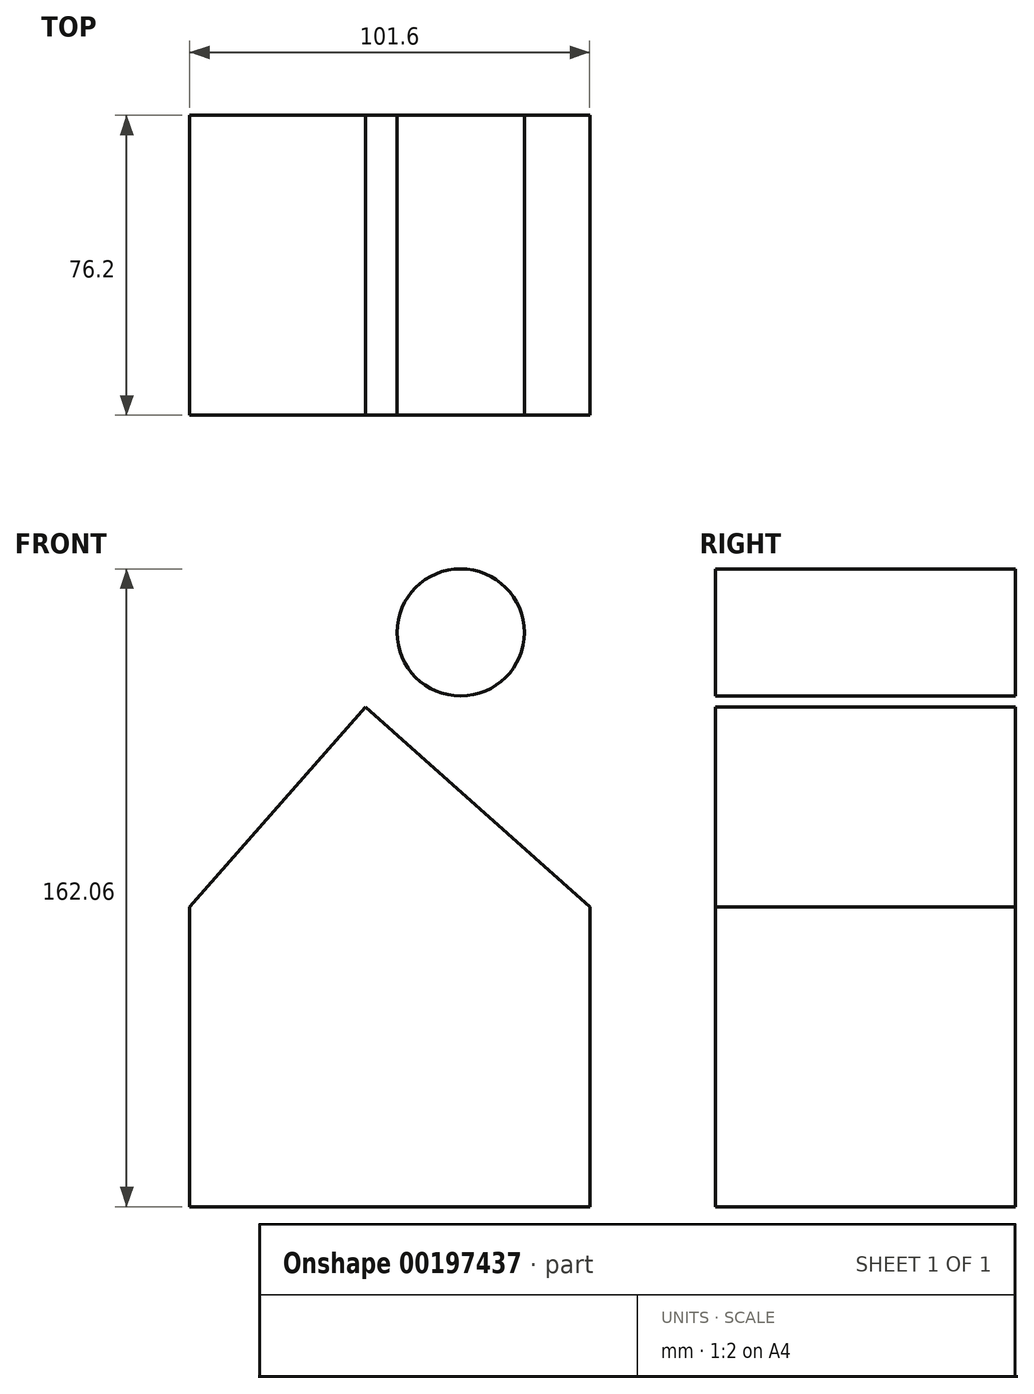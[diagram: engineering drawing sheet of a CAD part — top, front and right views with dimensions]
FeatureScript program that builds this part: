
annotation { "Feature Type Name" : "Feature", "Feature Type Description" : "" }
export const myFeature = defineFeature(function(context is Context, id is Id, definition is map)
    precondition{}
    {
        {
            var Q0;
            Q0=qCreatedBy(makeId("Front.planeOp"),FACE);
            var sketch = newSketch(context, id + "F0", { "sketchPlane" : qUnion([Q0])});
            skLineSegment(sketch, "E0.bottom", {"start": v(-44.6, 20.53) * mm, "end": v(57, 20.53) * mm});
            skLineSegment(sketch, "E0.top", {"start": v(-44.6, -55.67) * mm, "end": v(57, -55.67) * mm});
            skLineSegment(sketch, "E0.left", {"start": v(-44.6, 20.53) * mm, "end": v(-44.6, -55.67) * mm});
            skLineSegment(sketch, "E0.right", {"start": v(57, 20.53) * mm, "end": v(57, -55.67) * mm});
            skLineSegment(sketch, "E1", {"start": v(-44.6, 20.53) * mm, "end": v(0, 71.33) * mm});
            skLineSegment(sketch, "E2", {"start": v(0, 71.33) * mm, "end": v(57, 20.53) * mm});
            skCircle(sketch, "E3", {"center": v(24.22, 90.23) * mm, "radius": 16.16 * mm});
            skSolve(sketch);
        }
        {
            var Q0;
            Q0 = qSketchRegion(id + "F0", true);
            extrude(context, id + "F1", {"entities" : qUnion([Q0]), "depth" : 76.2 * mm});
        }
    });
